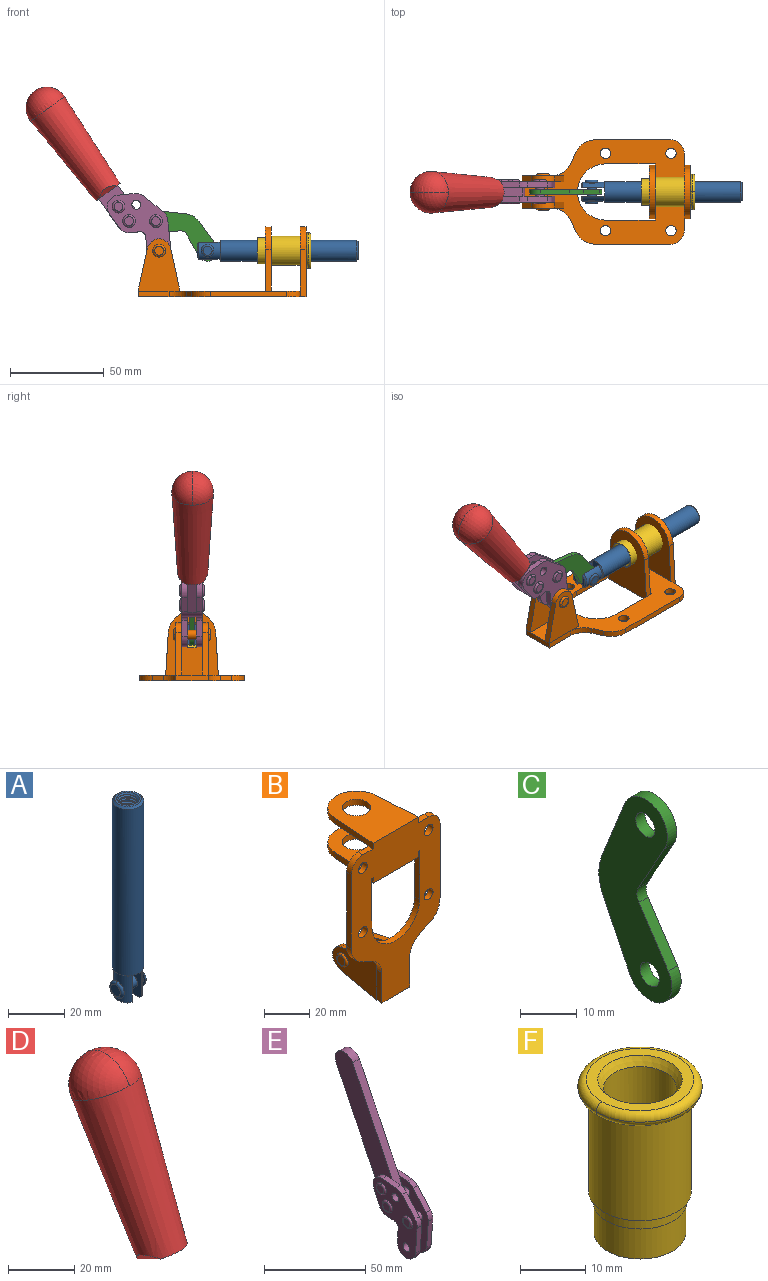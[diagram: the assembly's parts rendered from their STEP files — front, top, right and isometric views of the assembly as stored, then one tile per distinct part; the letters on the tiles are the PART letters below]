
ASSEMBLY  parts=6 mates=6
PART A: 48 faces, bbox 12.6x11.1x86.1 mm
  f0: torus R=2.41mm, axis (-1,0,0), area 15mm2, adj f30,f32,f34
  f1: torus R=2.41mm, axis (-1,0,0), area 15mm2, adj f29,f31,f33
  f2: cylinder r=5.54mm len=72.39mm, axis (0,0,1), area 2518.5mm2, adj f3,f4,f42,f43
  f3: cone r=5.54mm half-angle=45deg, axis (0,0,1), area 7.6mm2, adj f2,f5,f41
  f4: cone r=5.54mm half-angle=45deg, axis (0,0,-1), area 34.9mm2, adj f2,f39
  f5: cylinder r=5.08mm len=11.48mm, axis (0,0,1), area 108.3mm2, adj f3,f7,f8,f41
  f6: cylinder r=2.41mm len=4.83mm, axis (-1,0,0), area 71.2mm2, adj f40,f41
  f7: cylinder r=2.41mm len=4.83mm, axis (-1,0,0), area 7.6mm2, adj f5,f34
  f8: cone r=5.08mm half-angle=45deg, axis (0,0,1), area 10.6mm2, adj f5,f37,f41
  f9: cone r=3.98mm half-angle=45deg, axis (0,0,1), area 17.6mm2, adj f27,f39,f45,f46,f47
  f10: cylinder r=2.41mm len=4.83mm, axis (-1,0,0), area 7.6mm2, adj f33,f38
  f11: cylinder r=3.2mm len=6.4mm, axis (0,0,1), area 78.4mm2, adj f12,f28,f44,f45,f47
  f12: cylinder r=3.2mm len=6.4mm, axis (0,0,1), area 10.5mm2, adj f11,f13,f45,f47
  f13: cylinder r=3.2mm len=6.4mm, axis (0,0,1), area 10.5mm2, adj f12,f14,f45,f47
  f14: cylinder r=3.2mm len=6.4mm, axis (0,0,1), area 10.5mm2, adj f13,f15,f45,f47
  f15: cylinder r=3.2mm len=6.4mm, axis (0,0,1), area 10.5mm2, adj f14,f16,f45,f47
  f16: cylinder r=3.2mm len=6.4mm, axis (0,0,1), area 10.5mm2, adj f15,f17,f45,f47
  f17: cylinder r=3.2mm len=6.4mm, axis (0,0,1), area 10.5mm2, adj f16,f18,f45,f47
  f18: cylinder r=3.2mm len=6.4mm, axis (0,0,1), area 10.5mm2, adj f17,f19,f45,f47
  f19: cylinder r=3.2mm len=6.4mm, axis (0,0,1), area 10.5mm2, adj f18,f20,f45,f47
  f20: cylinder r=3.2mm len=6.4mm, axis (0,0,1), area 10.5mm2, adj f19,f21,f45,f47
  f21: cylinder r=3.2mm len=6.4mm, axis (0,0,1), area 10.5mm2, adj f20,f22,f45,f47
  f22: cylinder r=3.2mm len=6.4mm, axis (0,0,1), area 10.5mm2, adj f21,f23,f45,f47
  f23: cylinder r=3.2mm len=6.4mm, axis (0,0,1), area 10.5mm2, adj f22,f24,f45,f47
  f24: cylinder r=3.2mm len=6.4mm, axis (0,0,1), area 10.5mm2, adj f23,f25,f45,f47
  f25: cylinder r=3.2mm len=6.4mm, axis (0,0,1), area 10.5mm2, adj f24,f26,f45,f47
  f26: cylinder r=3.2mm len=6.4mm, axis (0,0,1), area 10.5mm2, adj f25,f27,f45,f47
  f27: cylinder r=3.2mm len=6.4mm, axis (0,0,1), area 7.4mm2, adj f9,f26,f45,f47
  f28: cone r=3.2mm half-angle=60deg, axis (0,0,1), area 37.2mm2, adj f11
  f29: plane 4.83x4.83mm, normal (-1,0,0), area 18.3mm2, adj f1,f31
  f30: plane 4.83x4.83mm, normal (1,0,0), area 18.3mm2, adj f0,f32
  f31: torus R=2.41mm, axis (-1,0,0), area 15mm2, adj f1,f29,f33
  f32: torus R=2.41mm, axis (-1,0,0), area 15mm2, adj f0,f30,f34
  f33: plane 6.83x6.83mm, normal (1,0,0), area 18.3mm2, adj f1,f10,f31
  f34: plane 6.83x6.83mm, normal (-1,0,0), area 18.3mm2, adj f0,f7,f32
  f35: cone r=5.08mm half-angle=45deg, axis (0,0,1), area 10.6mm2, adj f36,f38,f40
  f36: plane 7.25x1.97mm, normal (0,0,-1), area 10mm2, adj f35,f40
  f37: plane 7.25x1.97mm, normal (0,0,-1), area 10mm2, adj f8,f41
  f38: cylinder r=5.08mm len=11.48mm, axis (0,0,1), area 108.3mm2, adj f10,f35,f40,f42
  f39: plane 9.55x9.55mm, normal (0,0,1), area 22mm2, adj f4,f9
  f40: plane 12.76x10.09mm, normal (1,0,0), area 95.7mm2, adj f6,f35,f36,f38,f42,f43
  f41: plane 12.76x10.09mm, normal (-1,0,0), area 95.7mm2, adj f3,f5,f6,f8,f37,f43
  f42: cone r=5.54mm half-angle=45deg, axis (0,0,1), area 7.6mm2, adj f2,f38,f40
  f43: plane 11.07x4.7mm, normal (0,0,-1), area 50.4mm2, adj f2,f40,f41
  f44: plane 0.89x0.62mm, normal (-1,0,0), area 0.3mm2, adj f11,f45,f46,f47
  f45: bspline ~24.8x7.63mm, area 266.6mm2, adj f9,f11,f12,f13,f14,f15,f16,f17
  f46: bspline ~24.87x7.63mm, area 73.6mm2, adj f9,f44,f45,f47
  f47: bspline ~24.98x7.63mm, area 272.5mm2, adj f9,f11,f12,f13,f14,f15,f16,f17
PART B: 55 faces, bbox 55.7x37.4x89.8 mm
  f0: torus R=2.41mm, axis (-1,0,0), area 15mm2, adj f11,f15,f25
  f1: torus R=2.41mm, axis (-1,0,0), area 15mm2, adj f10,f12,f22
  f2: cylinder r=2.78mm len=5.56mm, axis (0,-1,0), area 54.2mm2, adj f30,f54
  f3: cylinder r=14.99mm len=29.97mm, axis (0,-1,0), area 145.9mm2, adj f30,f49,f53,f54
  f4: cylinder r=2.78mm len=5.56mm, axis (0,-1,0), area 54.2mm2, adj f30,f54
  f5: cylinder r=2.78mm len=5.56mm, axis (0,-1,0), area 54.2mm2, adj f30,f54
  f6: cylinder r=2.78mm len=5.56mm, axis (0,-1,0), area 54.2mm2, adj f30,f54
  f7: cylinder r=6.35mm len=12.7mm, axis (0,0,1), area 123.6mm2, adj f27,f51
  f8: cylinder r=6.35mm len=12.7mm, axis (0,0,-1), area 124.7mm2, adj f21,f35
  f9: cylinder r=2.41mm len=11.18mm, axis (-1,0,0), area 169.4mm2, adj f16,f19
  f10: plane 4.83x4.83mm, normal (1,0,0), area 18.3mm2, adj f1,f12
  f11: plane 4.83x4.83mm, normal (-1,0,0), area 18.3mm2, adj f0,f15
  f12: torus R=2.41mm, axis (-1,0,0), area 15mm2, adj f1,f10,f22
  f13: cylinder r=6.35mm len=12.41mm, axis (1,0,0), area 53.4mm2, adj f18,f19,f22,f23
  f14: cylinder r=6.35mm len=12.41mm, axis (-1,0,0), area 53.4mm2, adj f16,f17,f24,f25
  f15: torus R=2.41mm, axis (-1,0,0), area 15mm2, adj f0,f11,f25
  f16: plane 27.86x22.35mm, normal (1,0,0), area 425.4mm2, adj f9,f14,f17,f24,f30
  f17: plane 22.86x4.97mm, normal (0,0.21,0.98), area 72.5mm2, adj f14,f16,f25,f30
  f18: plane 22.86x4.97mm, normal (0,0.21,0.98), area 72.5mm2, adj f13,f19,f22,f30
  f19: plane 27.86x22.35mm, normal (-1,0,0), area 425.4mm2, adj f9,f13,f18,f23,f30
  f20: cylinder r=12.7mm len=25.35mm, axis (0,0,-1), area 119.8mm2, adj f21,f34,f35,f36
  f21: plane 34.21x28.07mm, normal (0,0,-1), area 702.4mm2, adj f8,f20,f30,f34,f36
  f22: plane 27.96x22.45mm, normal (1,0,0), area 407.2mm2, adj f1,f12,f13,f18,f23,f30,f42,f43
  f23: plane 22.86x4.97mm, normal (0,0.21,-0.98), area 72.5mm2, adj f13,f19,f22,f44
  f24: plane 22.86x4.97mm, normal (0,0.21,-0.98), area 72.5mm2, adj f14,f16,f25,f44
  f25: plane 27.86x22.35mm, normal (-1,0,0), area 407.1mm2, adj f0,f14,f15,f17,f24,f30,f45,f46
  f26: plane 3.1x0.95mm, normal (0,0,-1), area 2.7mm2, adj f30,f49,f50,f54
  f27: plane 34.21x28.07mm, normal (0,0,1), area 702.4mm2, adj f7,f28,f30,f50,f52
  f28: cylinder r=12.7mm len=25.35mm, axis (0,0,1), area 118.8mm2, adj f27,f50,f51,f52
  f29: plane 3.1x0.95mm, normal (0,0,-1), area 2.7mm2, adj f30,f52,f53,f54
  f30: plane 86.54x55.63mm, normal (0,1,0), area 2362.9mm2, adj f2,f3,f4,f5,f6,f16,f17,f18
  f31: plane 40.56x3.1mm, normal (-1,0,0), area 125.7mm2, adj f30,f32,f48,f54
  f32: cylinder r=7.11mm len=7.11mm, axis (0,-1,0), area 34.6mm2, adj f30,f31,f33,f54
  f33: plane 6.67x3.1mm, normal (0,0,1), area 20.4mm2, adj f30,f32,f34,f54
  f34: plane 25.39x3.13mm, normal (-1,0.06,0), area 79.5mm2, adj f20,f21,f33,f35,f54
  f35: plane 37.31x28.45mm, normal (0,0,1), area 789.9mm2, adj f8,f20,f34,f36,f54
  f36: plane 25.39x3.13mm, normal (1,0.06,0), area 79.5mm2, adj f20,f21,f35,f37,f54
  f37: plane 6.67x3.1mm, normal (0,0,1), area 20.4mm2, adj f30,f36,f38,f54
  f38: cylinder r=7.11mm len=7.11mm, axis (0,-1,0), area 34.6mm2, adj f30,f37,f39,f54
  f39: plane 40.56x3.1mm, normal (1,0,0), area 125.7mm2, adj f30,f38,f40,f54
  f40: cylinder r=11.18mm len=10.16mm, axis (0,-1,0), area 39.5mm2, adj f30,f39,f41,f54
  f41: plane 6.09x3.1mm, normal (0.42,0,-0.91), area 20.8mm2, adj f30,f40,f42,f54
  f42: cylinder r=11.18mm len=9.41mm, axis (0,-1,0), area 37.2mm2, adj f22,f30,f41,f43,f54
  f43: plane 16.5x3.1mm, normal (1,0,0), area 51.1mm2, adj f22,f42,f44,f54
  f44: plane 17.37x3.1mm, normal (0,0,-1), area 53.8mm2, adj f23,f24,f30,f43,f45,f54
  f45: plane 16.5x3.1mm, normal (-1,0,0), area 51.1mm2, adj f25,f44,f46,f54
  f46: cylinder r=11.18mm len=9.41mm, axis (0,-1,0), area 37.2mm2, adj f25,f30,f45,f47,f54
  f47: plane 6.09x3.1mm, normal (-0.42,0,-0.91), area 20.8mm2, adj f30,f46,f48,f54
  f48: cylinder r=11.18mm len=10.16mm, axis (0,-1,0), area 39.5mm2, adj f30,f31,f47,f54
  f49: plane 26.54x3.1mm, normal (-1,0,0), area 82.3mm2, adj f3,f26,f30,f54
  f50: plane 25.39x3.1mm, normal (1,0.06,0), area 78.8mm2, adj f26,f27,f28,f51,f54
  f51: plane 37.31x28.45mm, normal (0,0,-1), area 789.9mm2, adj f7,f28,f50,f52,f54
  f52: plane 25.39x3.1mm, normal (-1,0.06,0), area 78.8mm2, adj f27,f28,f29,f51,f54
  f53: plane 26.54x3.1mm, normal (1,0,0), area 82.3mm2, adj f3,f29,f30,f54
  f54: plane 89.66x55.63mm, normal (0,-1,0), area 2678.5mm2, adj f2,f3,f4,f5,f6,f26,f29,f31
PART C: 12 faces, bbox 2.3x18.2x42.8 mm
  f0: cylinder r=2.4mm len=4.8mm, axis (1,0,0), area 34.9mm2, adj f4,f11
  f1: cylinder r=10.41mm len=8.47mm, axis (1,0,0), area 20.2mm2, adj f4,f9,f10,f11
  f2: cylinder r=3.05mm len=3.16mm, axis (1,0,0), area 7.7mm2, adj f4,f6,f7,f11
  f3: cylinder r=2.4mm len=4.8mm, axis (1,0,0), area 34.9mm2, adj f4,f11
  f4: plane 42.81x18.23mm, normal (-1,0,0), area 414.1mm2, adj f0,f1,f2,f3,f5,f6,f7,f8
  f5: cylinder r=5.54mm len=10.67mm, axis (1,0,0), area 41.8mm2, adj f4,f6,f10,f11
  f6: plane 11.66x6.53mm, normal (0,-0.87,-0.49), area 30.9mm2, adj f2,f4,f5,f11
  f7: plane 11.17x7.33mm, normal (0,-0.84,0.55), area 30.9mm2, adj f2,f4,f8,f11
  f8: cylinder r=5.54mm len=10.51mm, axis (1,0,0), area 41.8mm2, adj f4,f7,f9,f11
  f9: plane 13.67x6.67mm, normal (0,0.9,-0.44), area 35.1mm2, adj f1,f4,f8,f11
  f10: plane 14.1x5.7mm, normal (0,0.93,0.37), area 35.1mm2, adj f1,f4,f5,f11
  f11: plane 42.81x18.23mm, normal (1,0,0), area 414.1mm2, adj f0,f1,f2,f3,f5,f6,f7,f8
PART D: 11 faces, bbox 22.3x42.6x64.5 mm
  f0: sphere r=11.13mm, area 411.4mm2, adj f1,f8
  f1: cone r=11.11mm half-angle=3.3deg, axis (0,0.44,0.9), area 3251.8mm2, adj f0,f7,f8,f9,f10
  f2: cylinder r=6.16mm len=11.7mm, axis (1,0,0), area 89.5mm2, adj f3,f4,f5,f6
  f3: plane 60.23x36.75mm, normal (-1,0,0), area 763.6mm2, adj f2,f4,f6,f10
  f4: plane 51.37x25.05mm, normal (0,0.9,-0.44), area 264.2mm2, adj f2,f3,f5,f10
  f5: plane 60.23x36.75mm, normal (1,0,0), area 763.6mm2, adj f2,f4,f6,f10
  f6: plane 51.37x25.05mm, normal (0,-0.9,0.44), area 264.2mm2, adj f2,f3,f5,f10
  f7: plane 9.95x5.95mm, normal (0.71,-0.31,-0.64), area 25.8mm2, adj f1,f10
  f8: sphere r=11.13mm, area 411.4mm2, adj f0,f1
  f9: plane 9.95x5.95mm, normal (-0.71,-0.31,-0.64), area 25.8mm2, adj f1,f10
  f10: plane 14.27x11.38mm, normal (0,-0.44,-0.9), area 106.7mm2, adj f1,f3,f4,f5,f6,f7,f9
PART E: 59 faces, bbox 12.9x60.2x99.6 mm
  f0: torus R=2.39mm, axis (-1,0,0), area 14.9mm2, adj f20,f43,f51
  f1: torus R=2.39mm, axis (-1,0,0), area 14.9mm2, adj f19,f42,f51
  f2: torus R=2.39mm, axis (-1,0,0), area 14.9mm2, adj f18,f35,f51
  f3: torus R=2.39mm, axis (-1,0,0), area 14.9mm2, adj f14,f17,f23
  f4: torus R=2.39mm, axis (-1,0,0), area 14.9mm2, adj f13,f16,f23
  f5: torus R=2.39mm, axis (-1,0,0), area 14.9mm2, adj f12,f15,f23
  f6: cylinder r=2.39mm len=4.78mm, axis (1,0,0), area 46.5mm2, adj f48,f50,f51
  f7: cylinder r=2.39mm len=4.78mm, axis (1,0,0), area 46.5mm2, adj f50,f51
  f8: cylinder r=6.35mm len=12.68mm, axis (1,0,0), area 61.8mm2, adj f38,f39,f50,f51
  f9: cylinder r=2.39mm len=4.78mm, axis (-1,0,0), area 70.5mm2, adj f46,f50
  f10: cylinder r=2.39mm len=4.78mm, axis (-1,0,0), area 46.5mm2, adj f23,f45,f46
  f11: cylinder r=2.39mm len=4.78mm, axis (-1,0,0), area 46.5mm2, adj f23,f46
  f12: plane 4.78x4.78mm, normal (1,0,0), area 17.9mm2, adj f5,f15
  f13: plane 4.78x4.78mm, normal (1,0,0), area 17.9mm2, adj f4,f16
  f14: plane 4.78x4.78mm, normal (1,0,0), area 17.9mm2, adj f3,f17
  f15: torus R=2.39mm, axis (-1,0,0), area 14.9mm2, adj f5,f12,f23
  f16: torus R=2.39mm, axis (-1,0,0), area 14.9mm2, adj f4,f13,f23
  f17: torus R=2.39mm, axis (-1,0,0), area 14.9mm2, adj f3,f14,f23
  f18: plane 4.78x4.78mm, normal (-1,0,0), area 17.9mm2, adj f2,f35
  f19: plane 4.78x4.78mm, normal (-1,0,0), area 17.9mm2, adj f1,f42
  f20: plane 4.78x4.78mm, normal (-1,0,0), area 17.9mm2, adj f0,f43
  f21: plane 2.26x0.2mm, normal (1,0,0), area 0.2mm2, adj f31,f44
  f22: plane 2.26x0.2mm, normal (-1,0,0), area 0.2mm2, adj f41,f44
  f23: plane 39.37x30.77mm, normal (1,0,0), area 565.5mm2, adj f3,f4,f5,f10,f11,f15,f16,f17
  f24: cylinder r=6.1mm len=4.15mm, axis (-1,0,0), area 14.7mm2, adj f23,f25,f32,f46
  f25: plane 10.25x9.01mm, normal (0,-0.75,0.66), area 42.3mm2, adj f23,f24,f26,f46
  f26: cylinder r=6.35mm len=4.64mm, axis (-1,0,0), area 15.6mm2, adj f23,f25,f27,f46
  f27: plane 15.84x3.1mm, normal (0,-1,-0.07), area 49.2mm2, adj f23,f26,f28,f46
  f28: cylinder r=6.35mm len=12.68mm, axis (-1,0,0), area 61.8mm2, adj f23,f27,f29,f46
  f29: plane 8.11x3.1mm, normal (0,1,0.07), area 25.2mm2, adj f23,f28,f30,f46
  f30: cylinder r=3.05mm len=3.25mm, axis (-1,0,0), area 14.8mm2, adj f23,f29,f31,f46
  f31: plane 5.99x3.1mm, normal (0,0.07,-1), area 18.6mm2, adj f21,f23,f30,f44,f46
  f32: plane 9.5x3.1mm, normal (0,-0.07,1), area 29.5mm2, adj f23,f24,f33,f46,f47
  f33: cylinder r=6.1mm len=8.63mm, axis (-1,0,0), area 39.1mm2, adj f23,f32,f34,f47
  f34: plane 8.65x3.96mm, normal (0,0.91,-0.42), area 29.5mm2, adj f23,f33,f44,f47
  f35: torus R=2.39mm, axis (-1,0,0), area 14.9mm2, adj f2,f18,f51
  f36: plane 10.25x9.01mm, normal (0,-0.75,0.66), area 42.3mm2, adj f37,f49,f50,f51
  f37: cylinder r=6.35mm len=4.64mm, axis (1,0,0), area 15.6mm2, adj f36,f38,f50,f51
  f38: plane 15.84x3.1mm, normal (0,-1,-0.07), area 49.2mm2, adj f8,f37,f50,f51
  f39: plane 8.11x3.1mm, normal (0,1,0.07), area 25.2mm2, adj f8,f40,f50,f51
  f40: cylinder r=3.05mm len=3.25mm, axis (1,0,0), area 14.8mm2, adj f39,f41,f50,f51
  f41: plane 5.99x3.1mm, normal (0,0.07,-1), area 18.6mm2, adj f22,f40,f44,f50,f51
  f42: torus R=2.39mm, axis (-1,0,0), area 14.9mm2, adj f1,f19,f51
  f43: torus R=2.39mm, axis (-1,0,0), area 14.9mm2, adj f0,f20,f51
  f44: cylinder r=6.35mm len=12.12mm, axis (-1,0,0), area 128.9mm2, adj f21,f22,f23,f31,f34,f41,f46,f47
  f45: plane 2.65x1.35mm, normal (1,0,0), area 1mm2, adj f10,f55
  f46: plane 39.08x20.42mm, normal (-1,0,0), area 412.5mm2, adj f9,f10,f11,f24,f25,f26,f27,f28
  f47: plane 77.62x39.82mm, normal (1,0,0), area 850mm2, adj f32,f33,f34,f44,f53,f54,f55
  f48: plane 2.65x1.35mm, normal (-1,0,0), area 1mm2, adj f6,f55
  f49: cylinder r=6.1mm len=4.15mm, axis (1,0,0), area 14.7mm2, adj f36,f50,f51,f56
  f50: plane 39.08x20.42mm, normal (1,0,0), area 412.5mm2, adj f6,f7,f8,f9,f36,f37,f38,f39
  f51: plane 39.37x30.77mm, normal (-1,0,0), area 565.5mm2, adj f0,f1,f2,f6,f7,f8,f35,f36
  f52: plane 8.65x3.96mm, normal (0,0.91,-0.42), area 29.5mm2, adj f44,f51,f57,f58
  f53: plane 68.49x33.4mm, normal (0,0.9,-0.44), area 358.1mm2, adj f44,f47,f54,f58
  f54: cylinder r=6.35mm len=12.06mm, axis (1,0,0), area 93.7mm2, adj f47,f53,f55,f58
  f55: plane 68.49x33.4mm, normal (0,-0.9,0.44), area 358.1mm2, adj f44,f45,f46,f47,f48,f50,f54,f58
  f56: plane 9.5x3.1mm, normal (0,-0.07,1), area 29.5mm2, adj f49,f50,f51,f57,f58
  f57: cylinder r=6.1mm len=8.63mm, axis (1,0,0), area 39.1mm2, adj f51,f52,f56,f58
  f58: plane 77.62x39.82mm, normal (-1,0,0), area 850mm2, adj f44,f52,f53,f54,f55,f56,f57
PART F: 15 faces, bbox 20.6x20.6x28.7 mm
  f0: torus R=8.26mm, axis (0,0,1), area 56.8mm2, adj f1,f10,f12
  f1: torus R=8.26mm, axis (0,0,1), area 56.8mm2, adj f0,f6,f13
  f2: cylinder r=5.59mm len=25.91mm, axis (0,0,1), area 909.6mm2, adj f3,f4
  f3: cone r=6.86mm half-angle=45deg, axis (0,0,-1), area 70.2mm2, adj f2,f14
  f4: cone r=6.47mm half-angle=30deg, axis (0,0,1), area 66.7mm2, adj f2,f13
  f5: cylinder r=7.04mm len=14.07mm, axis (0,0,1), area 252.6mm2, adj f11,f14
  f6: torus R=8.26mm, axis (0,0,1), area 56.8mm2, adj f1,f12,f13
  f7: cylinder r=7.16mm len=14.33mm, axis (0,0,1), area 91.5mm2, adj f9,f11
  f8: cylinder r=7.86mm len=18.42mm, axis (0,0,1), area 909.6mm2, adj f9,f10
  f9: plane 15.72x15.72mm, normal (0,0,-1), area 33mm2, adj f7,f8
  f10: plane 16.51x16.51mm, normal (0,0,-1), area 19.9mm2, adj f0,f8,f12
  f11: plane 14.33x14.33mm, normal (0,0,-1), area 5.7mm2, adj f5,f7
  f12: torus R=8.26mm, axis (0,0,1), area 56.8mm2, adj f0,f6,f10
  f13: plane 16.51x16.51mm, normal (0,0,1), area 82.7mm2, adj f1,f4,f6
  f14: plane 14.07x14.07mm, normal (0,0,-1), area 7.8mm2, adj f3,f5
PLACE A rot(axis=(-0.58,0.58,-0.58),120deg) t=(-23.24,0,30.57)mm
PLACE B rot(axis=(0.58,0.58,0.58),120deg) t=(-1.56,0,-18.66)mm fixed
PLACE C rot(axis=(0.46,-0.46,-0.76),105.5deg) t=(-33.11,0,-7.25)mm
PLACE D rot(axis=(-0.09,-0.09,0.99),90.4deg) t=(-14.99,-0.34,41.84)mm
PLACE E rot(axis=(-0.09,-0.09,0.99),90.4deg) t=(-14.99,0,41.84)mm
PLACE F rot(axis=(0,1,0),90deg) t=(-1.56,-24.61,5.96)mm
MATE revolute E.f4 <-> C.f5  axis (0,-1,0) through (-35.31,0,21.74)mm
MATE slider A.f2 <-> B.f7  axis (1,0,0) through (35.54,0,5.96)mm
MATE revolute C.f3 <-> A.f6  axis (0,-1,0) through (-7.77,0,5.96)mm
MATE fastened D.f2 <-> E.f54  axis (0,1,0) through (-94.46,-2.65,83.44)mm
MATE revolute E.f7 <-> B.f0  axis (0,1,0) through (-33.65,0,5.96)mm
MATE fastened F.f2 <-> B.f7  axis (1,0,0) through (44.83,0,5.96)mm
